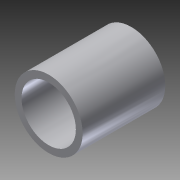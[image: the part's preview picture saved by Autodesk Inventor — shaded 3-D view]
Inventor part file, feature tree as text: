
AUTODESK INVENTOR PART (.ipt)
format: ipt  version: 2013 (Build 170138000, 138)  size: 83,968 bytes
history: native  units: in
note: dims shown in document units (in); Inventor stores cm internally (conversion verified against a paired STEP export)
features: extrude x1, sketch x1
ambient origin geometry x8: Origin, YZ Plane, XZ Plane, XY Plane, X Axis, Y Axis, Z Axis, Center Point
bodies: Solid1 (feature_tree)
feature tree (2):
  extrude  "Extrusion1"  Depth=0.5in
  sketch  "Sketch1"  dims[d0=0.625in d1=0.5in d2=0.77in d3=0.0in]
